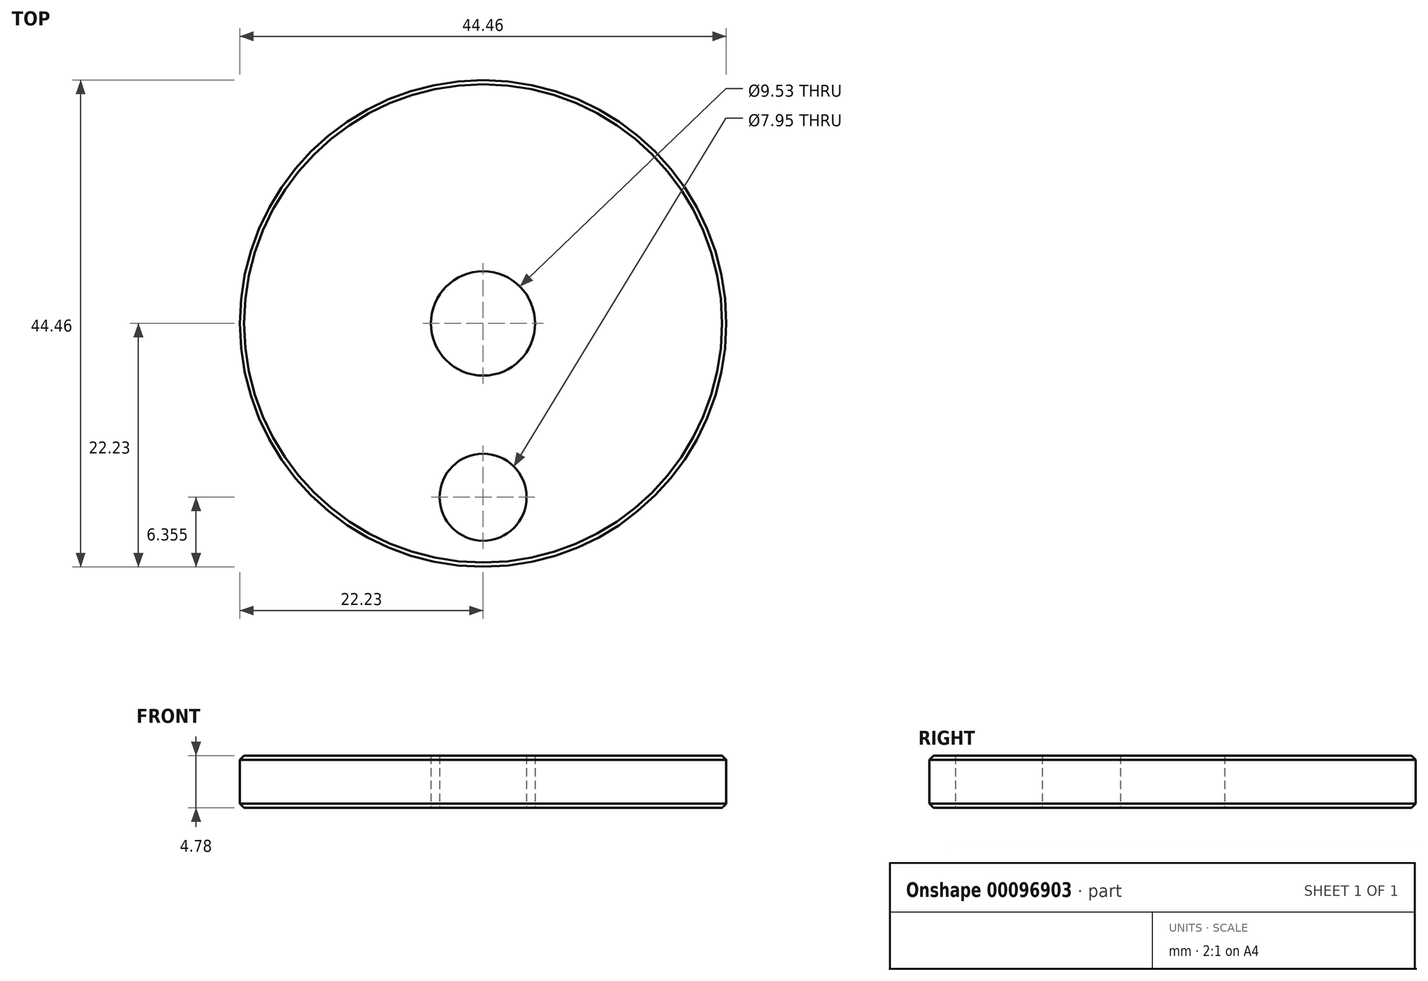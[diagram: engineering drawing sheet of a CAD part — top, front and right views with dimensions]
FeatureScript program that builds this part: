
annotation { "Feature Type Name" : "Feature", "Feature Type Description" : "" }
export const myFeature = defineFeature(function(context is Context, id is Id, definition is map)
    precondition{}
    {
        {
            var Q0;
            Q0=qCreatedBy(makeId("Top.planeOp"),FACE);
            var sketch = newSketch(context, id + "F0", { "sketchPlane" : qUnion([Q0])});
            skCircle(sketch, "E0", {"center": v(0, 0) * mm, "radius": 22.22 * mm});
            skCircle(sketch, "E1", {"center": v(0, 0) * mm, "radius": 4.76 * mm});
            skLineSegment(sketch, "E2", {"start": v(0, 0) * mm, "end": v(0, -31.75) * mm, "construction": true});
            skCircle(sketch, "E3", {"center": v(0, -15.88) * mm, "radius": 3.98 * mm});
            skSolve(sketch);
        }
        {
            var Q0;
            Q0 = qSketchRegion(id + "F0", true);
            extrude(context, id + "F1", {"entities" : qUnion([Q0]), "depth" : 4.78 * mm});
        }
        {
            var Q0;
            Q0=makeQuery(id+"F1.opExtrude","CAP_EDGE",EDGE,{"disambiguationData":[OSD([sQuery(id+"F0.wireOp",EDGE,"E0")])],"isStart":false});
            var Q1;
            Q1=makeQuery(id+"F1.opExtrude","CAP_EDGE",EDGE,{"disambiguationData":[OSD([sQuery(id+"F0.wireOp",EDGE,"E0")])],"isStart":true});
            chamfer(context, id + "F2", {"entities" : qUnion([Q0, Q1]), "width" : 0.38 * mm, "tangentPropagation" : true});
        }
    });
